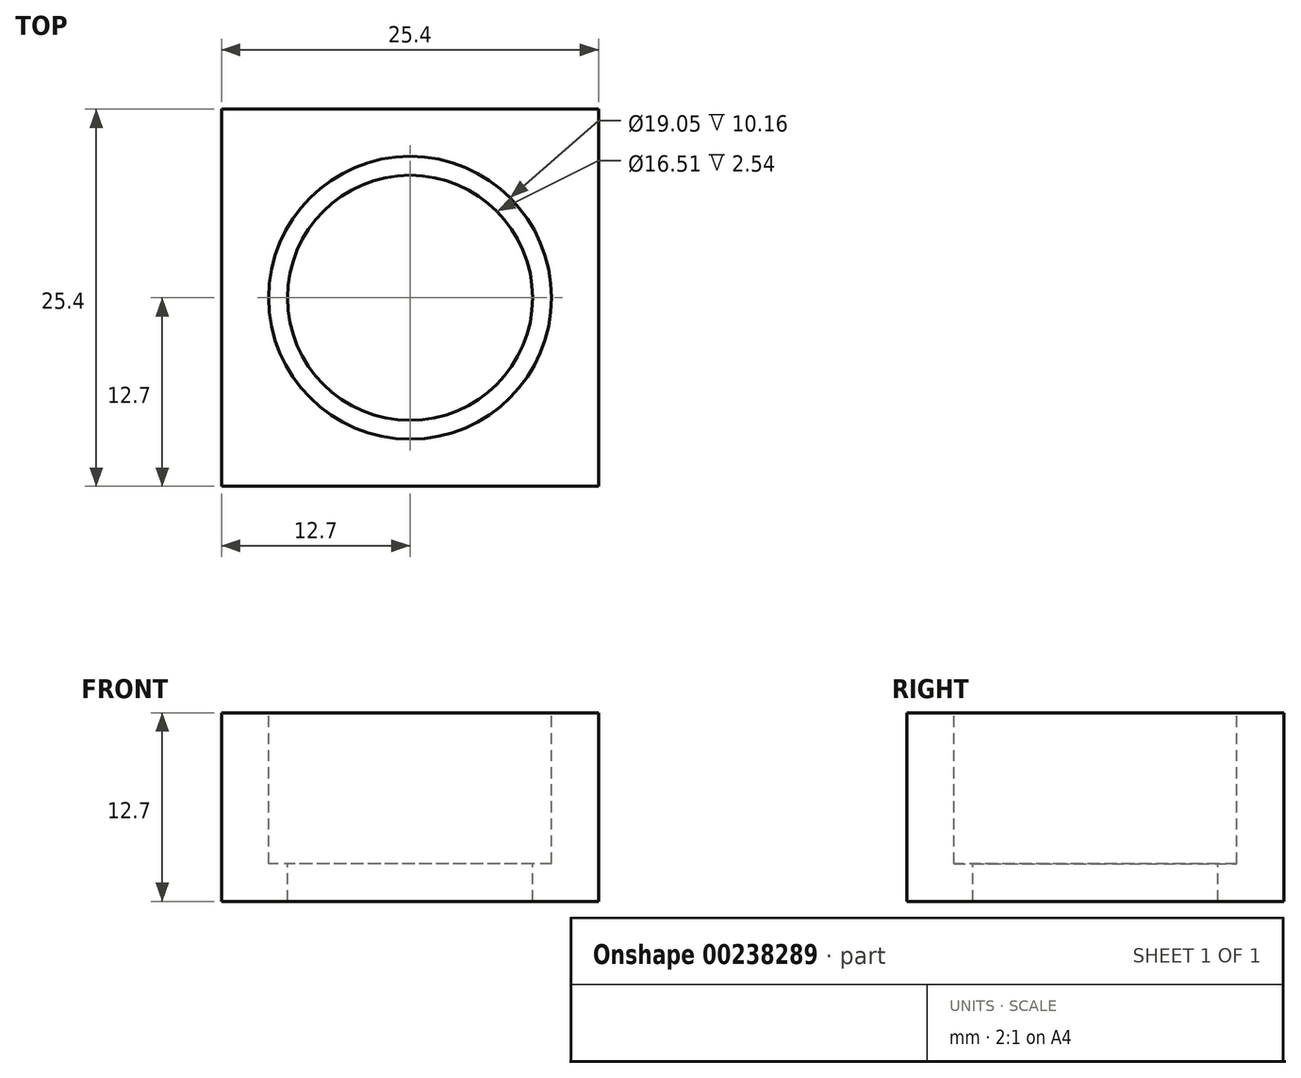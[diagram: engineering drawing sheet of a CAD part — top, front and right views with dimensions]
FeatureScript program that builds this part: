
annotation { "Feature Type Name" : "Feature", "Feature Type Description" : "" }
export const myFeature = defineFeature(function(context is Context, id is Id, definition is map)
    precondition{}
    {
        {
            var Q0;
            Q0=qCreatedBy(makeId("Top.planeOp"),FACE);
            var sketch = newSketch(context, id + "F0", { "sketchPlane" : qUnion([Q0])});
            skLineSegment(sketch, "E0.bottom", {"start": v(0, 0) * mm, "end": v(25.4, 0) * mm});
            skLineSegment(sketch, "E0.top", {"start": v(0, 25.4) * mm, "end": v(25.4, 25.4) * mm});
            skLineSegment(sketch, "E0.left", {"start": v(0, 0) * mm, "end": v(0, 25.4) * mm});
            skLineSegment(sketch, "E0.right", {"start": v(25.4, 0) * mm, "end": v(25.4, 25.4) * mm});
            skSolve(sketch);
        }
        {
            var Q0;
            Q0 = qSketchRegion(id + "F0", true);
            extrude(context, id + "F1", {"entities" : qUnion([Q0]), "depth" : 12.7 * mm});
        }
        {
            var Q0;
            Q0=makeQuery(id+"F1.opExtrude","CAP_FACE",FACE,{"disambiguationData":[OSD([sQuery(id+"F0.wireOp",EDGE,"E0.bottom"),sQuery(id+"F0.wireOp",EDGE,"E0.top"),sQuery(id+"F0.wireOp",EDGE,"E0.left"),sQuery(id+"F0.wireOp",EDGE,"E0.right")])],"isStart":false});
            var sketch = newSketch(context, id + "F2", { "sketchPlane" : qUnion([Q0])});
            skPoint(sketch, "E1.centerSnap0", {"position": v(0, 12.7) * mm});
            skPoint(sketch, "E1.centerSnap1", {"position": v(12.7, 25.4) * mm});
            skLineSegment(sketch, "E2", {"start": v(12.7, 25.4) * mm, "end": v(12.7, 0) * mm, "construction": true});
            skCircle(sketch, "E3", {"center": v(12.7, 12.7) * mm, "radius": 9.53 * mm});
            skSolve(sketch);
        }
        {
            var Q0;
            Q0 = qSketchRegion(id + "F2", true);
            extrude(context, id + "F3", {"entities" : qUnion([Q0]), "operationType" : NewBodyOperationType.REMOVE, "oppositeDirection" : true, "depth" : 10.16 * mm});
        }
        {
            var Q0;
            Q0=makeQuery(id+"F3.boolean.opBoolean","COPY",FACE,{"derivedFrom":makeQuery(id+"F3.opExtrude","CAP_FACE",FACE,{"disambiguationData":[OSD([sQuery(id+"F2.wireOp",EDGE,"E3")])],"isStart":false})});
            var sketch = newSketch(context, id + "F4", { "sketchPlane" : qUnion([Q0])});
            skCircle(sketch, "E4", {"center": v(12.7, 12.7) * mm, "radius": 8.26 * mm});
            skSolve(sketch);
        }
        {
            var Q0;
            Q0 = qSketchRegion(id + "F4", true);
            extrude(context, id + "F5", {"entities" : qUnion([Q0]), "operationType" : NewBodyOperationType.REMOVE, "endBound" : BoundingType.THROUGH_ALL, "oppositeDirection" : true, "depth" : 25.4 * mm});
        }
    });
